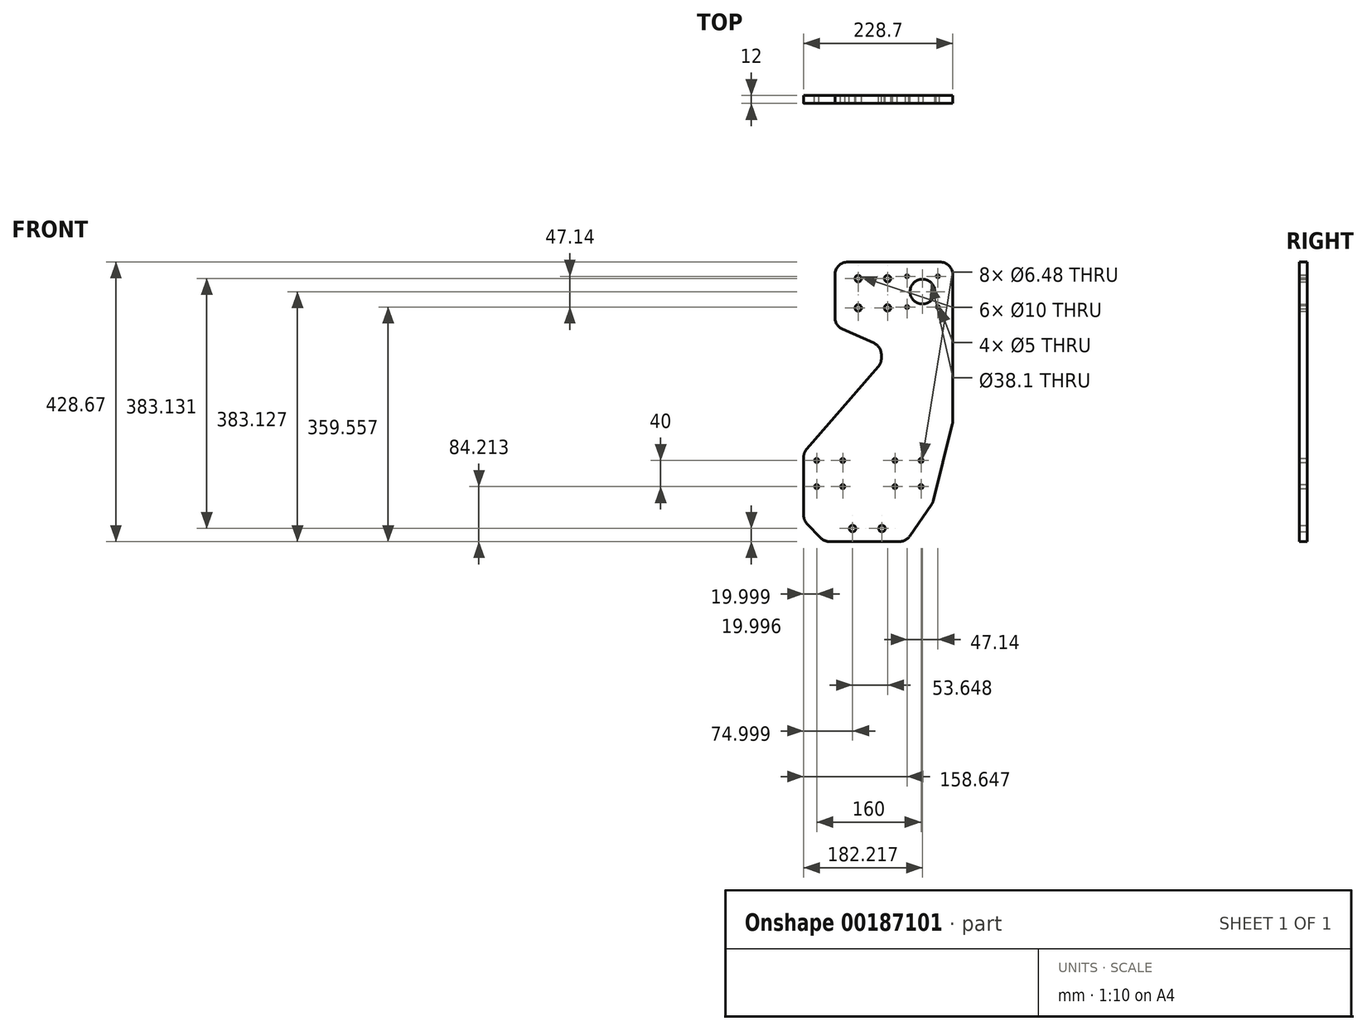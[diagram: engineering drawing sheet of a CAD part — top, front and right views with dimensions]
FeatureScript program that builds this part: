
annotation { "Feature Type Name" : "Feature", "Feature Type Description" : "" }
export const myFeature = defineFeature(function(context is Context, id is Id, definition is map)
    precondition{}
    {
        {
            var Q0;
            Q0=qCreatedBy(makeId("Front.planeOp"),FACE);
            var sketch = newSketch(context, id + "F0", { "sketchPlane" : qUnion([Q0])});
            skLineSegment(sketch, "E0.top", {"start": v(85.23, 205) * mm, "end": v(25.3, 205) * mm});
            skPoint(sketch, "E0.middle", {"position": v(0, 0) * mm});
            skLineSegment(sketch, "E1", {"start": v(135.36, -38.58) * mm, "end": v(135.36, 185) * mm});
            skLineSegment(sketch, "E2", {"start": v(115.36, 205) * mm, "end": v(85.23, 205) * mm});
            skCircle(sketch, "E3", {"center": v(-73.34, -139.46) * mm, "radius": 3.24 * mm});
            skCircle(sketch, "E4", {"center": v(-73.34, -99.46) * mm, "radius": 3.24 * mm});
            skCircle(sketch, "E5", {"center": v(-33.34, -99.46) * mm, "radius": 3.24 * mm});
            skCircle(sketch, "E6", {"center": v(-33.34, -139.46) * mm, "radius": 3.24 * mm});
            skCircle(sketch, "E7", {"center": v(46.66, -99.46) * mm, "radius": 3.24 * mm});
            skCircle(sketch, "E8", {"center": v(46.66, -139.46) * mm, "radius": 3.24 * mm});
            skCircle(sketch, "E9", {"center": v(86.66, -139.46) * mm, "radius": 3.24 * mm});
            skCircle(sketch, "E10", {"center": v(86.66, -99.46) * mm, "radius": 3.24 * mm});
            skCircle(sketch, "E11", {"center": v(-18.34, -203.67) * mm, "radius": 5 * mm});
            skCircle(sketch, "E12", {"center": v(26.66, -203.67) * mm, "radius": 5 * mm});
            skCircle(sketch, "E13", {"center": v(-9.7, 179.46) * mm, "radius": 5 * mm});
            skCircle(sketch, "E14", {"center": v(35.3, 179.46) * mm, "radius": 5 * mm});
            skCircle(sketch, "E15", {"center": v(-9.7, 134.46) * mm, "radius": 5 * mm});
            skCircle(sketch, "E16", {"center": v(35.3, 134.46) * mm, "radius": 5 * mm});
            skCircle(sketch, "E17", {"center": v(65.3, 183.03) * mm, "radius": 2.5 * mm});
            skCircle(sketch, "E18", {"center": v(112.45, 183.03) * mm, "radius": 2.5 * mm});
            skCircle(sketch, "E19", {"center": v(65.3, 135.89) * mm, "radius": 2.5 * mm});
            skCircle(sketch, "E20", {"center": v(112.45, 135.89) * mm, "radius": 2.5 * mm});
            skCircle(sketch, "E21", {"center": v(88.88, 159.46) * mm, "radius": 19.05 * mm});
            skArc(sketch, "E22.filletArc", {"start": v(135.36, 185) * mm, "mid": v(129.5, 199.14) * mm, "end": v(115.36, 205) * mm});
            skLineSegment(sketch, "E23", {"start": v(25.3, 205) * mm, "end": v(25.3, 205) * mm});
            skLineSegment(sketch, "E24", {"start": v(25.3, 205) * mm, "end": v(10.35, 205) * mm});
            skLineSegment(sketch, "E25", {"start": v(0.04, 128.58) * mm, "end": v(-2.03, 128.58) * mm});
            skLineSegment(sketch, "E26", {"start": v(-93.34, -94.44) * mm, "end": v(-93.34, -135.08) * mm});
            skLineSegment(sketch, "E27", {"start": v(10.35, 205) * mm, "end": v(-13, 205) * mm});
            skLineSegment(sketch, "E28", {"start": v(-93.34, -135.08) * mm, "end": v(-93.34, -183.04) * mm});
            skLineSegment(sketch, "E29", {"start": v(-53.7, -223.67) * mm, "end": v(53.23, -223.67) * mm});
            skLineSegment(sketch, "E30", {"start": v(105.34, -161.24) * mm, "end": v(134.76, -43.42) * mm});
            skLineSegment(sketch, "E31", {"start": v(-87.83, -196.83) * mm, "end": v(-68.18, -217.46) * mm});
            skArc(sketch, "E32.filletArc", {"start": v(-93.34, -183.04) * mm, "mid": v(-91.91, -190.47) * mm, "end": v(-87.83, -196.83) * mm});
            skArc(sketch, "E33.filletArc", {"start": v(-68.18, -217.46) * mm, "mid": v(-61.58, -222.06) * mm, "end": v(-53.7, -223.67) * mm});
            skLineSegment(sketch, "E34", {"start": v(69.67, -215.05) * mm, "end": v(102.39, -167.77) * mm});
            skArc(sketch, "E35.filletArc", {"start": v(53.23, -223.67) * mm, "mid": v(62.51, -221.39) * mm, "end": v(69.67, -215.05) * mm});
            skArc(sketch, "E36.filletArc", {"start": v(102.39, -167.77) * mm, "mid": v(104.16, -164.64) * mm, "end": v(105.34, -161.24) * mm});
            skArc(sketch, "E37.filletArc", {"start": v(134.76, -43.42) * mm, "mid": v(135.21, -41.02) * mm, "end": v(135.36, -38.58) * mm});
            skLineSegment(sketch, "E38", {"start": v(-13, 205) * mm, "end": v(-25.42, 205) * mm});
            skPoint(sketch, "E39.visualSharp", {"position": v(-45.42, 205) * mm});
            skArc(sketch, "E39.filletArc", {"start": v(-25.42, 205) * mm, "mid": v(-39.56, 199.14) * mm, "end": v(-45.42, 185) * mm});
            skArc(sketch, "E40.filletArc", {"start": v(-51.19, -36.8) * mm, "mid": v(-50.2, -36.05) * mm, "end": v(-49.27, -35.23) * mm});
            skLineSegment(sketch, "E41", {"start": v(-88.42, -81.3) * mm, "end": v(20.86, 44.08) * mm});
            skPoint(sketch, "E42.visualSharp", {"position": v(33.64, 58.75) * mm});
            skPoint(sketch, "E43.visualSharp", {"position": v(-93.34, -86.95) * mm});
            skArc(sketch, "E43.filletArc", {"start": v(-88.42, -81.3) * mm, "mid": v(-92.07, -87.42) * mm, "end": v(-93.34, -94.44) * mm});
            skLineSegment(sketch, "E44", {"start": v(-45.42, 185) * mm, "end": v(-45.42, 120.1) * mm});
            skLineSegment(sketch, "E45", {"start": v(-33.52, 101.81) * mm, "end": v(13.88, 80.84) * mm});
            skLineSegment(sketch, "E46", {"start": v(25.78, 62.55) * mm, "end": v(25.78, 57.23) * mm});
            skPoint(sketch, "E47.visualSharp", {"position": v(-45.42, 107.08) * mm});
            skArc(sketch, "E47.filletArc", {"start": v(-45.42, 120.1) * mm, "mid": v(-42.18, 109.2) * mm, "end": v(-33.52, 101.81) * mm});
            skPoint(sketch, "E48.visualSharp", {"position": v(25.78, 75.57) * mm});
            skArc(sketch, "E48.filletArc", {"start": v(25.78, 62.55) * mm, "mid": v(22.54, 73.46) * mm, "end": v(13.88, 80.84) * mm});
            skPoint(sketch, "E49.visualSharp", {"position": v(25.78, 49.73) * mm});
            skArc(sketch, "E49.filletArc", {"start": v(20.86, 44.08) * mm, "mid": v(24.51, 50.2) * mm, "end": v(25.78, 57.23) * mm});
            skSolve(sketch);
        }
        {
            var Q0;
            Q0=makeQuery(id+"F0.imprint","IMPRINT",FACE,{"disambiguationData":[TD([[makeQuery(id+"F0.imprint","IMPRINT",EDGE,{"derivedFrom":sQuery(id+"F0.wireOp",EDGE,"E0.top")}),1.0]])]});
            extrude(context, id + "F1", {"entities" : qUnion([Q0]), "depth" : 12 * mm});
        }
    });
